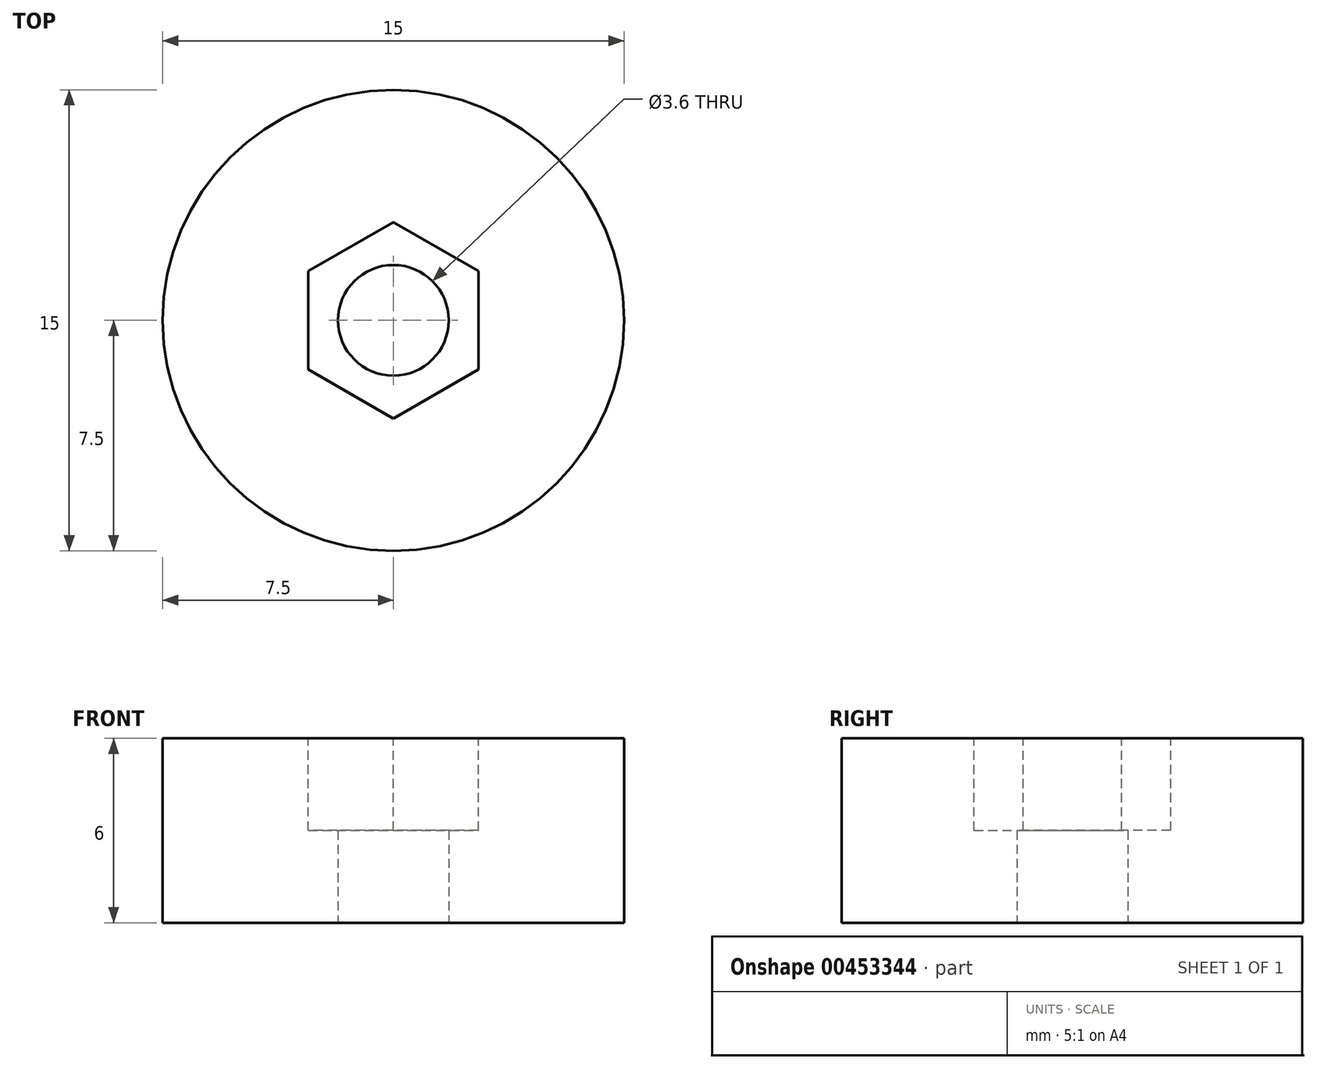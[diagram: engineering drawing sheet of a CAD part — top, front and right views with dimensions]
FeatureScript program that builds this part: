
annotation { "Feature Type Name" : "Feature", "Feature Type Description" : "" }
export const myFeature = defineFeature(function(context is Context, id is Id, definition is map)
    precondition{}
    {
        {
            var Q0;
            Q0=qCreatedBy(makeId("Top.planeOp"),FACE);
            var sketch = newSketch(context, id + "F0", { "sketchPlane" : qUnion([Q0])});
            skCircle(sketch, "E0", {"center": v(0, 0) * mm, "radius": 7.5 * mm});
            skCircle(sketch, "E1", {"center": v(0, 0) * mm, "radius": 1.8 * mm});
            skSolve(sketch);
        }
        {
            var Q0;
            Q0 = qSketchRegion(id + "F0", true);
            extrude(context, id + "F1", {"entities" : qUnion([Q0]), "depth" : 6 * mm});
        }
        {
            var Q0;
            Q0=makeQuery(id+"F1.opExtrude","CAP_FACE",FACE,{"disambiguationData":[OSD([sQuery(id+"F0.wireOp",EDGE,"E0"),sQuery(id+"F0.wireOp",EDGE,"E1")])],"isStart":false});
            var sketch = newSketch(context, id + "F2", { "sketchPlane" : qUnion([Q0])});
            skCircle(sketch, "E2.cCircle", {"center": v(0, 0) * mm, "radius": 3.2 * mm, "construction": true});
            skLineSegment(sketch, "E2.0", {"start": v(0, 3.2) * mm, "end": v(2.77, 1.6) * mm});
            skLineSegment(sketch, "E2.1", {"start": v(2.77, 1.6) * mm, "end": v(2.77, -1.6) * mm});
            skLineSegment(sketch, "E2.2", {"start": v(2.77, -1.6) * mm, "end": v(0, -3.2) * mm});
            skLineSegment(sketch, "E2.3", {"start": v(0, -3.2) * mm, "end": v(-2.77, -1.6) * mm});
            skLineSegment(sketch, "E2.4", {"start": v(-2.77, -1.6) * mm, "end": v(-2.77, 1.6) * mm});
            skLineSegment(sketch, "E2.5", {"start": v(-2.77, 1.6) * mm, "end": v(0, 3.2) * mm});
            skSolve(sketch);
        }
        {
            var Q0;
            Q0 = qSketchRegion(id + "F2", true);
            extrude(context, id + "F3", {"entities" : qUnion([Q0]), "operationType" : NewBodyOperationType.REMOVE, "oppositeDirection" : true, "depth" : 3 * mm});
        }
    });
